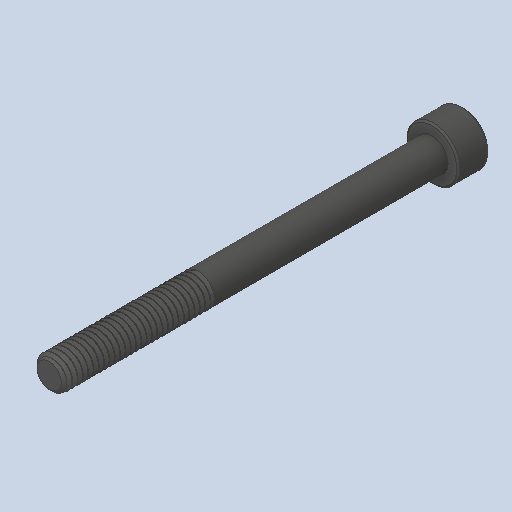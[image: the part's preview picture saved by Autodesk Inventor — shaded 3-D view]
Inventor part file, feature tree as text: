
AUTODESK INVENTOR PART (.ipt)
format: ipt  version: 2023 (Build 270158000, 158)  size: 666,624 bytes
history: native  units: in
note: dims shown in document units (in); Inventor stores cm internally (conversion verified against a paired STEP export)
features: chamfer x1
ambient origin geometry x8: Origin, YZ Plane, XZ Plane, XY Plane, X Axis, Y Axis, Z Axis, Center Point
bodies: Solid1 (feature_tree)
feature tree (1):
  chamfer  "Chamfer2"  [1 undecoded]
note: 1 required parameter value undecoded (feature->parameter linkage not recoverable at this tier; creation-order binding heuristic only, values carry confidence <= 0.55)
